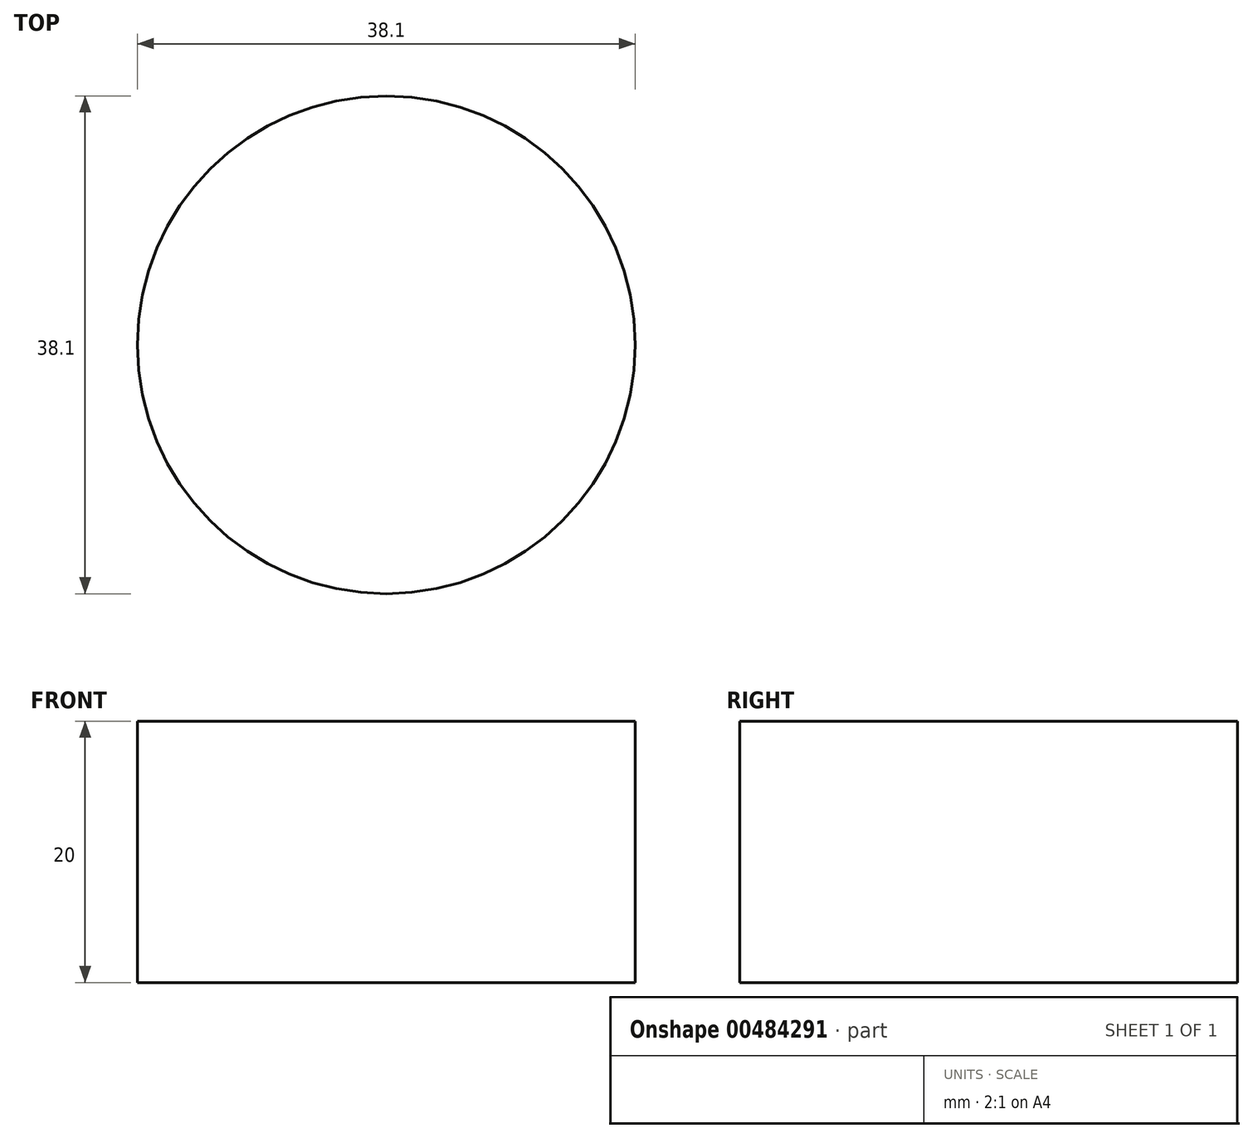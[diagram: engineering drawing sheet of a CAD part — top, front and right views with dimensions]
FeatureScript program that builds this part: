
annotation { "Feature Type Name" : "Feature", "Feature Type Description" : "" }
export const myFeature = defineFeature(function(context is Context, id is Id, definition is map)
    precondition{}
    {
        {
            var Q0;
            Q0=qCreatedBy(makeId("Top.planeOp"),FACE);
            var sketch = newSketch(context, id + "F0", { "sketchPlane" : qUnion([Q0])});
            skCircle(sketch, "E0", {"center": v(0, 0) * mm, "radius": 19.05 * mm});
            skSolve(sketch);
        }
        {
            var Q0;
            Q0=makeQuery(id+"F0.imprint","IMPRINT",FACE,{"disambiguationData":[TD([[makeQuery(id+"F0.imprint","IMPRINT",EDGE,{"derivedFrom":sQuery(id+"F0.wireOp",EDGE,"E0")}),1.0]])]});
            extrude(context, id + "F1", {"entities" : qUnion([Q0]), "oppositeDirection" : true, "depth" : 20 * mm});
        }
    });
